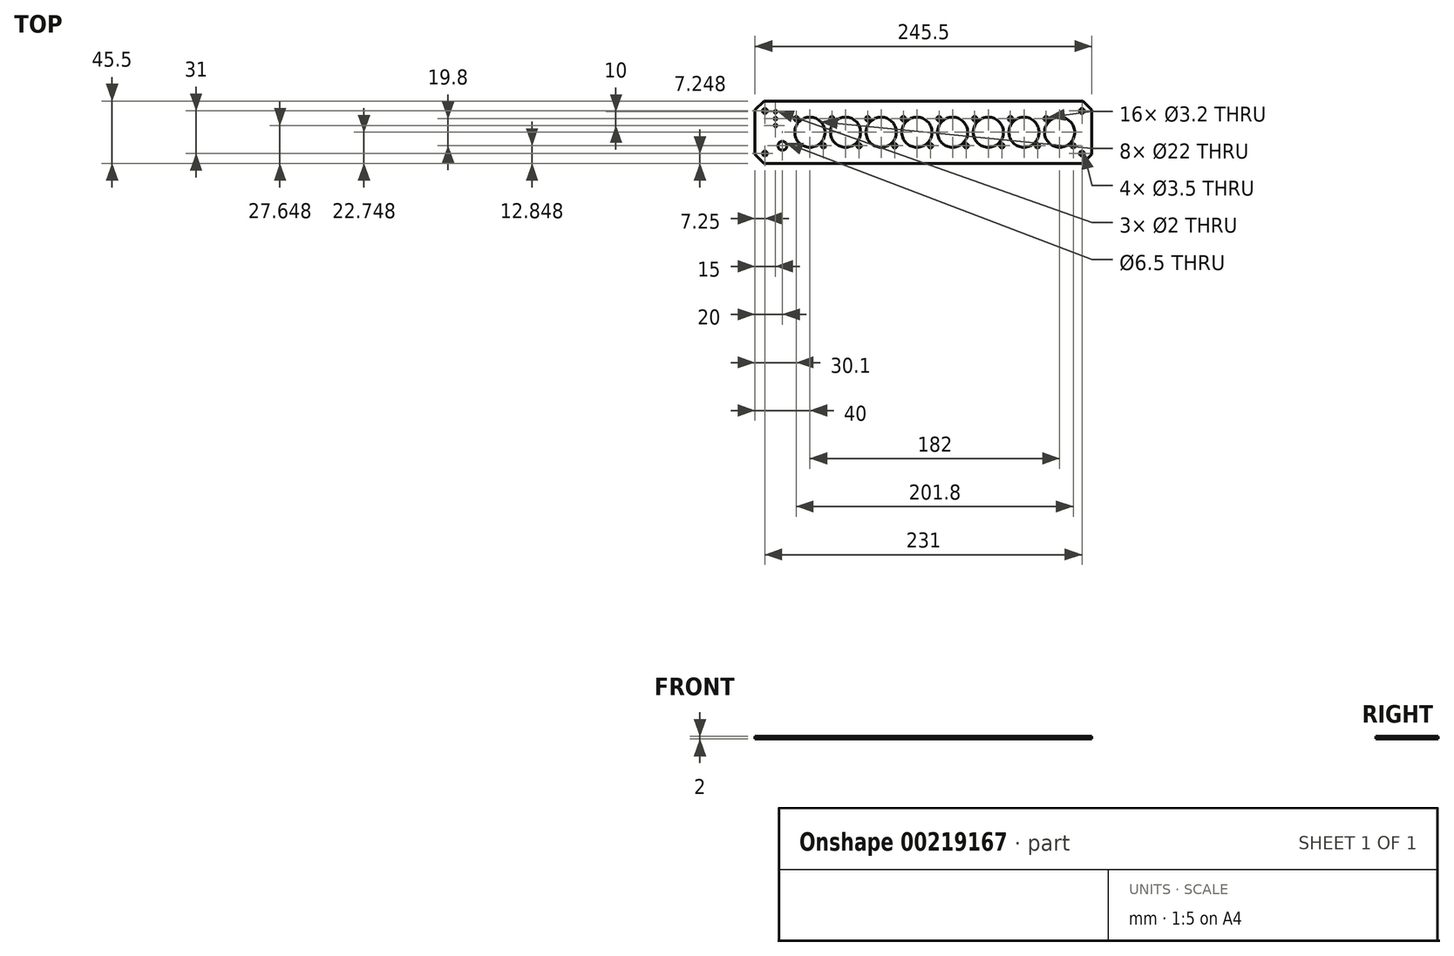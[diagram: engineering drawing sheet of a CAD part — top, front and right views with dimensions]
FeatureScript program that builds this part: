
annotation { "Feature Type Name" : "Feature", "Feature Type Description" : "" }
export const myFeature = defineFeature(function(context is Context, id is Id, definition is map)
    precondition{}
    {
        {
            var Q0;
            Q0=qCreatedBy(makeId("Top.planeOp"),FACE);
            var sketch = newSketch(context, id + "F0", { "sketchPlane" : qUnion([Q0])});
            skCircle(sketch, "E0.3.0.0", {"center": v(-74.6, -2.07) * mm, "radius": 11 * mm});
            skCircle(sketch, "E1.3.0.0", {"center": v(-84.5, 7.83) * mm, "radius": 1.6 * mm});
            skCircle(sketch, "E1.3.0.1", {"center": v(-64.7, -11.97) * mm, "radius": 1.6 * mm});
            skCircle(sketch, "E2.1.0.0", {"center": v(-48.6, -2.07) * mm, "radius": 11 * mm});
            skCircle(sketch, "E2.1.0.1", {"center": v(-58.5, 7.83) * mm, "radius": 1.6 * mm});
            skCircle(sketch, "E2.1.0.2", {"center": v(-38.7, -11.97) * mm, "radius": 1.6 * mm});
            skCircle(sketch, "E2.2.0.0", {"center": v(-22.6, -2.07) * mm, "radius": 11 * mm});
            skCircle(sketch, "E2.2.0.1", {"center": v(-32.5, 7.83) * mm, "radius": 1.6 * mm});
            skCircle(sketch, "E2.2.0.2", {"center": v(-12.7, -11.97) * mm, "radius": 1.6 * mm});
            skCircle(sketch, "E2.3.0.0", {"center": v(3.4, -2.07) * mm, "radius": 11 * mm});
            skCircle(sketch, "E2.3.0.1", {"center": v(-6.5, 7.83) * mm, "radius": 1.6 * mm});
            skCircle(sketch, "E2.3.0.2", {"center": v(13.3, -11.97) * mm, "radius": 1.6 * mm});
            skCircle(sketch, "E2.4.0.0", {"center": v(29.4, -2.07) * mm, "radius": 11 * mm});
            skCircle(sketch, "E2.4.0.1", {"center": v(19.5, 7.83) * mm, "radius": 1.6 * mm});
            skCircle(sketch, "E2.4.0.2", {"center": v(39.3, -11.97) * mm, "radius": 1.6 * mm});
            skCircle(sketch, "E2.5.0.0", {"center": v(55.4, -2.07) * mm, "radius": 11 * mm});
            skCircle(sketch, "E2.5.0.1", {"center": v(45.5, 7.83) * mm, "radius": 1.6 * mm});
            skCircle(sketch, "E2.5.0.2", {"center": v(65.3, -11.97) * mm, "radius": 1.6 * mm});
            skCircle(sketch, "E2.6.0.0", {"center": v(81.4, -2.07) * mm, "radius": 11 * mm});
            skCircle(sketch, "E2.6.0.1", {"center": v(71.5, 7.83) * mm, "radius": 1.6 * mm});
            skCircle(sketch, "E2.6.0.2", {"center": v(91.3, -11.97) * mm, "radius": 1.6 * mm});
            skCircle(sketch, "E2.7.0.0", {"center": v(107.4, -2.07) * mm, "radius": 11 * mm});
            skCircle(sketch, "E2.7.0.1", {"center": v(97.5, 7.83) * mm, "radius": 1.6 * mm});
            skCircle(sketch, "E2.7.0.2", {"center": v(117.3, -11.97) * mm, "radius": 1.6 * mm});
            skLineSegment(sketch, "E3", {"start": v(-108.1, 20.68) * mm, "end": v(124.4, 20.68) * mm});
            skLineSegment(sketch, "E4", {"start": v(-114.6, 14.18) * mm, "end": v(-114.6, -18.32) * mm});
            skLineSegment(sketch, "E5", {"start": v(-108.1, -24.82) * mm, "end": v(124.4, -24.82) * mm});
            skLineSegment(sketch, "E6", {"start": v(130.9, 14.18) * mm, "end": v(130.9, -18.32) * mm});
            skLineSegment(sketch, "E7", {"start": v(-108.1, 20.68) * mm, "end": v(-114.6, 14.18) * mm});
            skLineSegment(sketch, "E8", {"start": v(-114.6, -18.32) * mm, "end": v(-108.1, -24.82) * mm});
            skLineSegment(sketch, "E9", {"start": v(130.9, -18.32) * mm, "end": v(124.4, -24.82) * mm});
            skLineSegment(sketch, "E10", {"start": v(130.9, 14.18) * mm, "end": v(124.4, 20.68) * mm});
            skPoint(sketch, "E11.left.start.orphan", {"position": v(-110.61, 20.68) * mm});
            skCircle(sketch, "E12", {"center": v(-107.36, 13.43) * mm, "radius": 1.75 * mm});
            skLineSegment(sketch, "E13.bottom", {"start": v(-107.36, 13.43) * mm, "end": v(123.64, 13.43) * mm, "construction": true});
            skLineSegment(sketch, "E13.top", {"start": v(-107.36, -17.57) * mm, "end": v(123.64, -17.57) * mm, "construction": true});
            skLineSegment(sketch, "E13.left", {"start": v(-107.36, 13.43) * mm, "end": v(-107.36, -17.57) * mm, "construction": true});
            skLineSegment(sketch, "E13.right", {"start": v(123.64, 13.43) * mm, "end": v(123.64, -17.57) * mm, "construction": true});
            skCircle(sketch, "E14", {"center": v(-107.36, -17.57) * mm, "radius": 1.75 * mm});
            skCircle(sketch, "E15", {"center": v(123.64, 13.43) * mm, "radius": 1.75 * mm});
            skCircle(sketch, "E16", {"center": v(123.64, -17.57) * mm, "radius": 1.75 * mm});
            skCircle(sketch, "E17", {"center": v(-99.6, 7.83) * mm, "radius": 1 * mm});
            skCircle(sketch, "E18", {"center": v(-94.6, -11.97) * mm, "radius": 3.25 * mm});
            skCircle(sketch, "E19", {"center": v(-99.6, 12.83) * mm, "radius": 1 * mm});
            skCircle(sketch, "E20", {"center": v(-99.6, 2.83) * mm, "radius": 1 * mm});
            skSolve(sketch);
        }
        {
            var Q0;
            Q0=makeQuery(id+"F0.imprint","IMPRINT",FACE,{"disambiguationData":[TD([[makeQuery(id+"F0.imprint","IMPRINT",EDGE,{"derivedFrom":sQuery(id+"F0.wireOp",EDGE,"E0.3.0.0")}),-1.0]])]});
            extrude(context, id + "F1", {"entities" : qUnion([Q0]), "depth" : 2 * mm});
        }
    });
